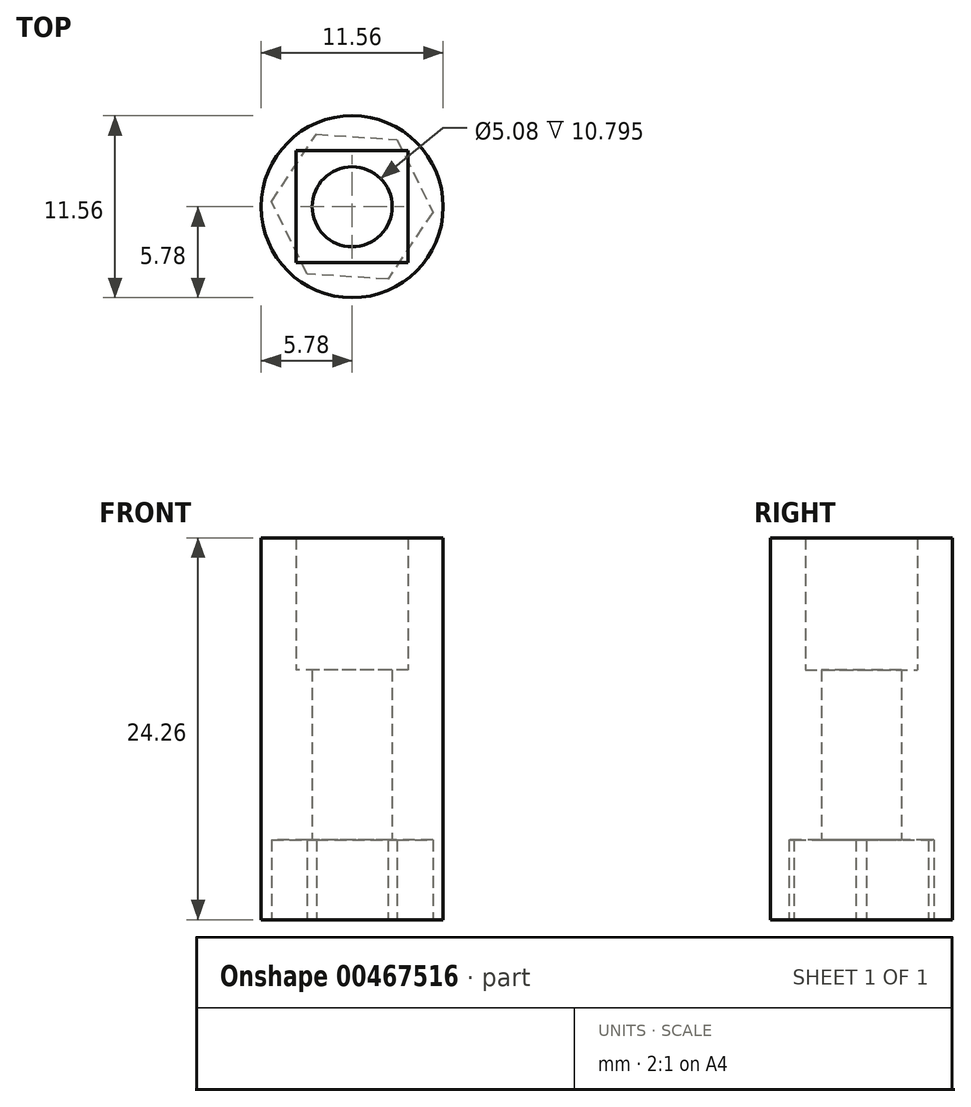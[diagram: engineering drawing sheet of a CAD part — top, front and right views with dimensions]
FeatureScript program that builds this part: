
annotation { "Feature Type Name" : "Feature", "Feature Type Description" : "" }
export const myFeature = defineFeature(function(context is Context, id is Id, definition is map)
    precondition{}
    {
        {
            var Q0;
            Q0=qCreatedBy(makeId("Top.planeOp"),FACE);
            var sketch = newSketch(context, id + "F0", { "sketchPlane" : qUnion([Q0])});
            skCircle(sketch, "E0.cCircle", {"center": v(0, 0) * mm, "radius": 4.45 * mm, "construction": true});
            skLineSegment(sketch, "E0.0", {"start": v(5.12, -0.34) * mm, "end": v(2.27, -4.6) * mm});
            skLineSegment(sketch, "E0.1", {"start": v(2.27, -4.6) * mm, "end": v(-2.85, -4.27) * mm});
            skLineSegment(sketch, "E0.2", {"start": v(-2.85, -4.27) * mm, "end": v(-5.12, 0.34) * mm});
            skLineSegment(sketch, "E0.3", {"start": v(-5.12, 0.34) * mm, "end": v(-2.27, 4.6) * mm});
            skLineSegment(sketch, "E0.4", {"start": v(-2.27, 4.6) * mm, "end": v(2.85, 4.27) * mm});
            skLineSegment(sketch, "E0.5", {"start": v(2.85, 4.27) * mm, "end": v(5.12, -0.34) * mm});
            skPoint(sketch, "E0.0.midPoint", {"position": v(3.7, -2.47) * mm});
            skCircle(sketch, "E1", {"center": v(0, 0) * mm, "radius": 5.78 * mm});
            skSolve(sketch);
        }
        {
            var Q0;
            Q0 = qSketchRegion(id + "F0", true);
            var Q1;
            Q1=makeQuery(id+"F0.imprint","IMPRINT",FACE,{"disambiguationData":[TD([[makeQuery(id+"F0.imprint","IMPRINT",EDGE,{"derivedFrom":sQuery(id+"F0.wireOp",EDGE,"E0.0")}),-1.0]])]});
            extrude(context, id + "F1", {"entities" : qUnion([Q0, Q1]), "depth" : 15.88 * mm});
        }
        {
            var Q0;
            Q0=makeQuery(id+"F0.imprint","IMPRINT",FACE,{"disambiguationData":[TD([[makeQuery(id+"F0.imprint","IMPRINT",EDGE,{"derivedFrom":sQuery(id+"F0.wireOp",EDGE,"E0.0")}),-1.0]])]});
            extrude(context, id + "F2", {"entities" : qUnion([Q0]), "operationType" : NewBodyOperationType.REMOVE, "depth" : 5.08 * mm});
        }
        {
            var Q0;
            Q0=sQuery(id+"F0.wireOp",VERTEX,"E1.center");
            var Q1;
            Q1=makeQuery(id+"F1.opExtrude","SWEPT_BODY",BODY,{"disambiguationData":[OSD([sQuery(id+"F0.wireOp",EDGE,"E1")])]});
            hole(context, id + "F3", {"style" : HoleStyle.SIMPLE, "endStyle" : HoleEndStyle.THROUGH, "oppositeDirection" : true, "holeDiameter" : 5.08 * mm, "isTappedThrough" : true, "tappedDepth" : 12.7 * mm, "tapClearance" : 3, "locations" : qUnion([Q0]), "scope" : qUnion([Q1])});
        }
        {
            var Q0;
            Q0=makeQuery(id+"F1.opExtrude","CAP_FACE",FACE,{"disambiguationData":[OSD([sQuery(id+"F0.wireOp",EDGE,"E1")])],"isStart":false});
            var sketch = newSketch(context, id + "F4", { "sketchPlane" : qUnion([Q0])});
            skSolve(sketch);
        }
        {
            var Q0;
            {var subQ0=sQuery(id+"F0.wireOp",EDGE,"E1");Q0=makeQuery(id+"F4.imprint","IMPRINT",FACE,{"disambiguationData":[TD([[makeQuery(id+"F4.imprint","IMPRINT",EDGE,{"derivedFrom":makeQuery(id+"F1.opExtrude","CAP_EDGE",EDGE,{"disambiguationData":[OSD([subQ0])],"isStart":false})}),1.0]])]});}
            var sketch = newSketch(context, id + "F5", { "sketchPlane" : qUnion([Q0])});
            skCircle(sketch, "E2.0", {"center": v(0, 0) * mm, "radius": 2.54 * mm});
            skLineSegment(sketch, "E3.bottom", {"start": v(3.56, -3.56) * mm, "end": v(-3.56, -3.56) * mm});
            skLineSegment(sketch, "E3.top", {"start": v(3.56, 3.56) * mm, "end": v(-3.56, 3.56) * mm});
            skLineSegment(sketch, "E3.left", {"start": v(3.56, -3.56) * mm, "end": v(3.56, 3.56) * mm});
            skLineSegment(sketch, "E3.right", {"start": v(-3.56, -3.56) * mm, "end": v(-3.56, 3.56) * mm});
            skCircle(sketch, "E4.0", {"center": v(0, 0) * mm, "radius": 5.78 * mm});
            skSolve(sketch);
        }
        {
            var Q0;
            Q0 = qSketchRegion(id + "F5", true);
            extrude(context, id + "F6", {"entities" : qUnion([Q0]), "operationType" : NewBodyOperationType.ADD, "depth" : 8.38 * mm});
        }
    });
